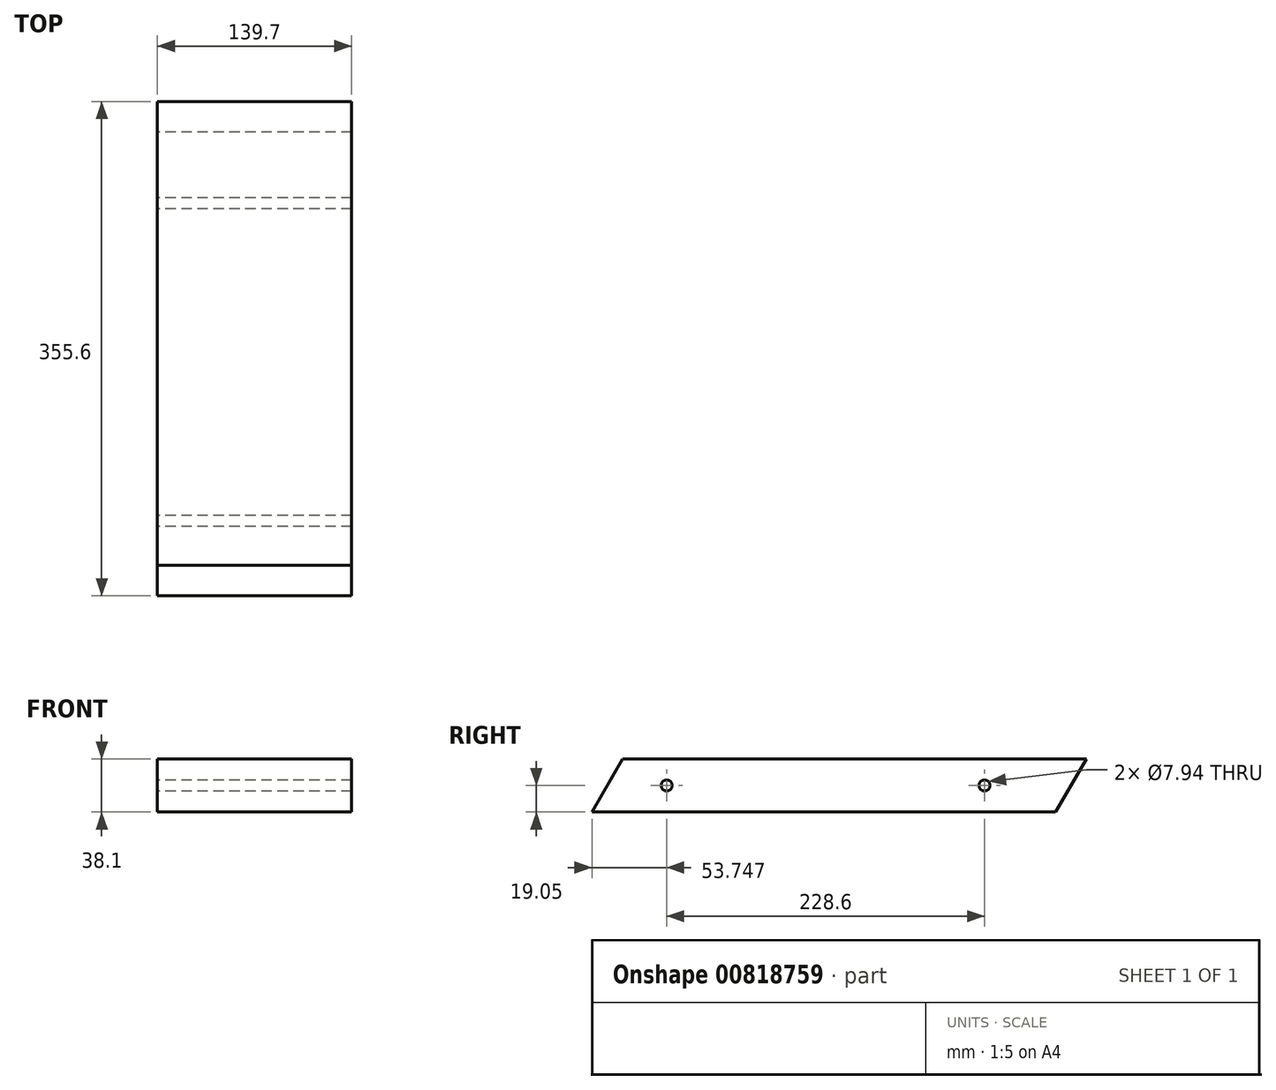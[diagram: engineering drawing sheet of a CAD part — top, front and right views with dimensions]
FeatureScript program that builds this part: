
annotation { "Feature Type Name" : "Feature", "Feature Type Description" : "" }
export const myFeature = defineFeature(function(context is Context, id is Id, definition is map)
    precondition{}
    {
        {
            var Q0;
            Q0=qCreatedBy(makeId("Front.planeOp"),FACE);
            var sketch = newSketch(context, id + "F0", { "sketchPlane" : qUnion([Q0])});
            skLineSegment(sketch, "E0.bottom", {"start": v(-69.85, 19.05) * mm, "end": v(69.85, 19.05) * mm});
            skLineSegment(sketch, "E0.top", {"start": v(-69.85, -19.05) * mm, "end": v(69.85, -19.05) * mm});
            skLineSegment(sketch, "E0.left", {"start": v(-69.85, 19.05) * mm, "end": v(-69.85, -19.05) * mm});
            skLineSegment(sketch, "E0.right", {"start": v(69.85, 19.05) * mm, "end": v(69.85, -19.05) * mm});
            skSolve(sketch);
        }
        {
            var Q0;
            Q0=qSketchRegion(id+"F0",true);
            extrude(context, id + "F1", {"entities" : qUnion([Q0]), "depth" : 177.8 * mm, "offsetDistance" : 25.4 * mm, "hasSecondDirection" : true, "secondDirectionOppositeDirection" : true, "secondDirectionDepth" : 177.8 * mm});
        }
        {
            var Q0;
            Q0=makeQuery(id+"F1.opExtrude","SWEPT_FACE",FACE,{"disambiguationData":[OSD([sQuery(id+"F0.wireOp",EDGE,"E0.left")])]});
            var sketch = newSketch(context, id + "F2", { "sketchPlane" : qUnion([Q0])});
            skLineSegment(sketch, "E1", {"start": v(-177.8, 19.05) * mm, "end": v(-155.8, -19.05) * mm});
            skLineSegment(sketch, "E2", {"start": v(-155.8, -19.05) * mm, "end": v(-177.8, -19.05) * mm});
            skLineSegment(sketch, "E3", {"start": v(-177.8, -19.05) * mm, "end": v(-177.8, 19.05) * mm});
            skLineSegment(sketch, "E4", {"start": v(177.8, 19.05) * mm, "end": v(155.8, 19.05) * mm});
            skLineSegment(sketch, "E5", {"start": v(155.8, 19.05) * mm, "end": v(177.8, -19.05) * mm});
            skLineSegment(sketch, "E6", {"start": v(177.8, -19.05) * mm, "end": v(177.8, 19.05) * mm});
            skSolve(sketch);
        }
        {
            var Q0;
            Q0=qSketchRegion(id+"F2",true);
            extrude(context, id + "F3", {"entities" : qUnion([Q0]), "operationType" : NewBodyOperationType.REMOVE, "endBound" : BoundingType.UP_TO_NEXT, "oppositeDirection" : true, "depth" : 25.4 * mm, "offsetDistance" : 25.4 * mm});
        }
        {
            var Q0;
            Q0=makeQuery(id+"F1.opExtrude","SWEPT_FACE",FACE,{"disambiguationData":[OSD([sQuery(id+"F0.wireOp",EDGE,"E0.left")])]});
            var sketch = newSketch(context, id + "F4", { "sketchPlane" : qUnion([Q0])});
            skCircle(sketch, "E7", {"center": v(-104.55, 0) * mm, "radius": 3.97 * mm});
            skCircle(sketch, "E8", {"center": v(124.05, 0) * mm, "radius": 3.97 * mm});
            skSolve(sketch);
        }
        {
            var Q0;
            Q0 = qSketchRegion(id + "F4", true);
            extrude(context, id + "F5", {"entities" : qUnion([Q0]), "operationType" : NewBodyOperationType.REMOVE, "endBound" : BoundingType.THROUGH_ALL, "oppositeDirection" : true, "depth" : 25.4 * mm, "offsetDistance" : 25.4 * mm});
        }
    });
